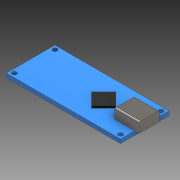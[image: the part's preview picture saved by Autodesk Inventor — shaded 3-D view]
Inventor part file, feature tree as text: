
AUTODESK INVENTOR PART (.ipt)
format: ipt  version: 2017 (Build 210142000, 142)  size: 124,416 bytes
history: native  units: mm
features: extrude x3, sketch x2, fillet x1
ambient origin geometry x8: Origin, YZ Plane, XZ Plane, XY Plane, X Axis, Y Axis, Z Axis, Center Point
bodies: Solid1 (feature_tree)
feature tree (6):
  extrude  "Extrusion1"  Depth=18.44mm
  sketch  "Sketch2"  dims[d2=1.7mm d3=1.5mm d4=1.5mm d5=1.5mm d6=1.5mm d7=1.53mm d8=0.0mm d9=45.0deg d10=6.5mm d11=15.65mm d12=9.25mm d13=7.6mm d14=1.73mm d15=3.75mm d16=0.0mm d17=0.8mm d18=0.0mm d19=0.5mm]
  extrude  "Extrusion2"  Depth=0.5mm
  extrude  "Extrusion3"  Depth=0.5mm
  fillet  "Fillet1"  Radius=1.5mm
  sketch  "Sketch1"  dims[d0=43.38mm d1=18.44mm]
